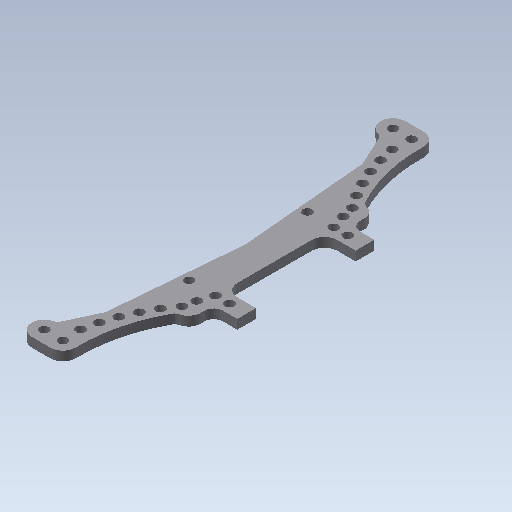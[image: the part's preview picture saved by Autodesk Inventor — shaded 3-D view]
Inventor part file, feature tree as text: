
AUTODESK INVENTOR PART (.ipt)
format: ipt  version: 2020 (Build 240168000, 168)  size: 201,728 bytes
history: native  units: mm
features: extrude x1, mirror x1, sketch x1
ambient origin geometry x8: Origin, YZ Plane, XZ Plane, XY Plane, X Axis, Y Axis, Z Axis, Center Point
bodies: Body1 (feature_tree)
feature tree (3):
  extrude  "Extrusion2"  TaperAngle=0.0deg  [1 undecoded]
  mirror  "Mirror1"
  sketch  "Sketch1"  dims[d0=28.0mm d1=0.0mm d2=2.0mm d3=4.0mm d4=12.0mm d5=0.0mm d6=10.0mm d8=0.872665mm d9=3.490659mm d10=4.0mm d11=4.0mm d12=50.0mm d13=4.0mm d14=3.0mm d15=54.0mm d16=1.797689mm d17=4.625123mm d18=27.35mm d19=12.4mm d20=3.0mm d21=56.0mm d22=0.0mm d23=60.0mm d25=4.625123mm d28=3.0mm d29=3.0mm d30=3.0mm d31=5.5mm d32=4.5mm d34=19.0mm d35=3.0mm d36=4.5mm d38=13.0mm d39=3.0mm d40=6.0mm d42=3.0mm d43=3.0mm d44=2.0mm d47=3.0mm d48=0.0mm]
note: 1 required parameter value undecoded (feature->parameter linkage not recoverable at this tier; creation-order binding heuristic only, values carry confidence <= 0.55)
